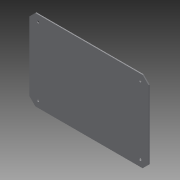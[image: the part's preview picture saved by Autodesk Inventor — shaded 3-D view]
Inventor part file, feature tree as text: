
AUTODESK INVENTOR PART (.ipt)
format: ipt  version: 2014 (Build 180170000, 170)  size: 407,040 bytes
history: native  units: mm
features: extrude x3, sketch x3, chamfer x1, other x1
ambient origin geometry x8: Origin, YZ Plane, XZ Plane, XY Plane, X Axis, Y Axis, Z Axis, Center Point
bodies: Solid1 (feature_tree)
feature tree (8):
  extrude  "Extrusion1"  Depth=95.0mm
  extrude  "Extrusion2"  Depth=1.2mm TaperAngle=0.0deg
  extrude  "Extrusion3"  Depth=80.0mm
  chamfer  "Chamfer1"  Distance=3.0mm
  sketch  "Sketch1"  dims[d0=140.0mm d1=95.0mm]
  sketch  "Sketch2"  dims[d2=1.2mm d3=0.0mm d37=1.2mm d38=0.0mm]
  other  "Image2"
  sketch  "Sketch3"  dims[d40=120.0mm d41=80.0mm d42=3.0mm d43=3.0mm d44=3.0mm d45=17.05mm d46=0.0mm d47=7.0mm d48=2.0mm d49=45.0deg]
